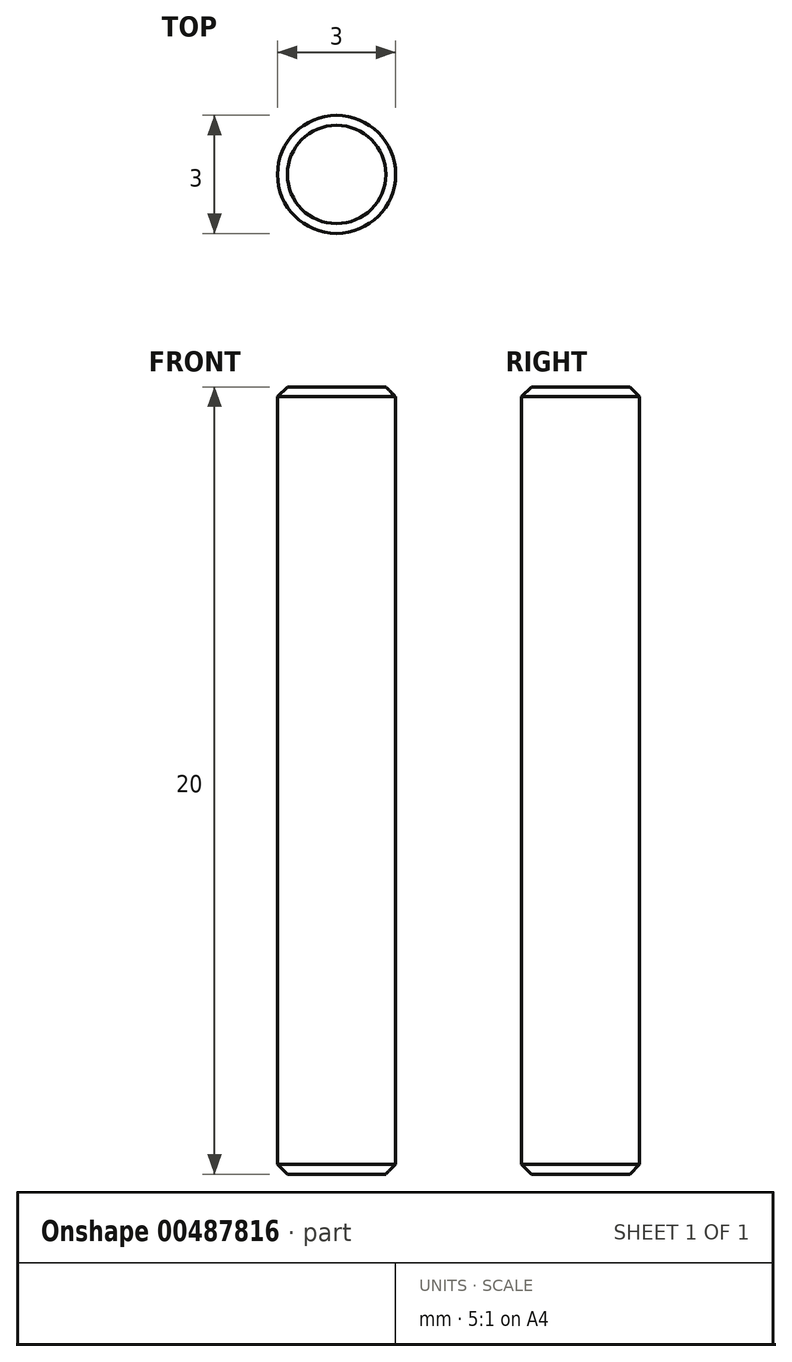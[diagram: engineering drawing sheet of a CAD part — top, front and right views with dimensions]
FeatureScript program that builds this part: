
annotation { "Feature Type Name" : "Feature", "Feature Type Description" : "" }
export const myFeature = defineFeature(function(context is Context, id is Id, definition is map)
    precondition{}
    {
        {
            var Q0;
            Q0=qCreatedBy(makeId("Top.planeOp"),FACE);
            var sketch = newSketch(context, id + "F0", { "sketchPlane" : qUnion([Q0])});
            skCircle(sketch, "E0", {"center": v(0, 0) * mm, "radius": 1.5 * mm});
            skSolve(sketch);
        }
        {
            var Q0;
            Q0=qSketchRegion(id+"F0",true);
            extrude(context, id + "F1", {"entities" : qUnion([Q0]), "depth" : 20 * mm, "offsetDistance" : 25 * mm});
        }
        {
            var Q0;
            Q0=makeQuery(id+"F1.opExtrude","CAP_FACE",FACE,{"disambiguationData":[OSD([sQuery(id+"F0.wireOp",EDGE,"E0")])],"isStart":false});
            var Q1;
            Q1=makeQuery(id+"F1.opExtrude","CAP_EDGE",EDGE,{"disambiguationData":[OSD([sQuery(id+"F0.wireOp",EDGE,"E0")])],"isStart":true});
            chamfer(context, id + "F2", {"entities" : qUnion([Q0, Q1]), "width" : .25 * mm, "tangentPropagation" : true});
        }
    });
